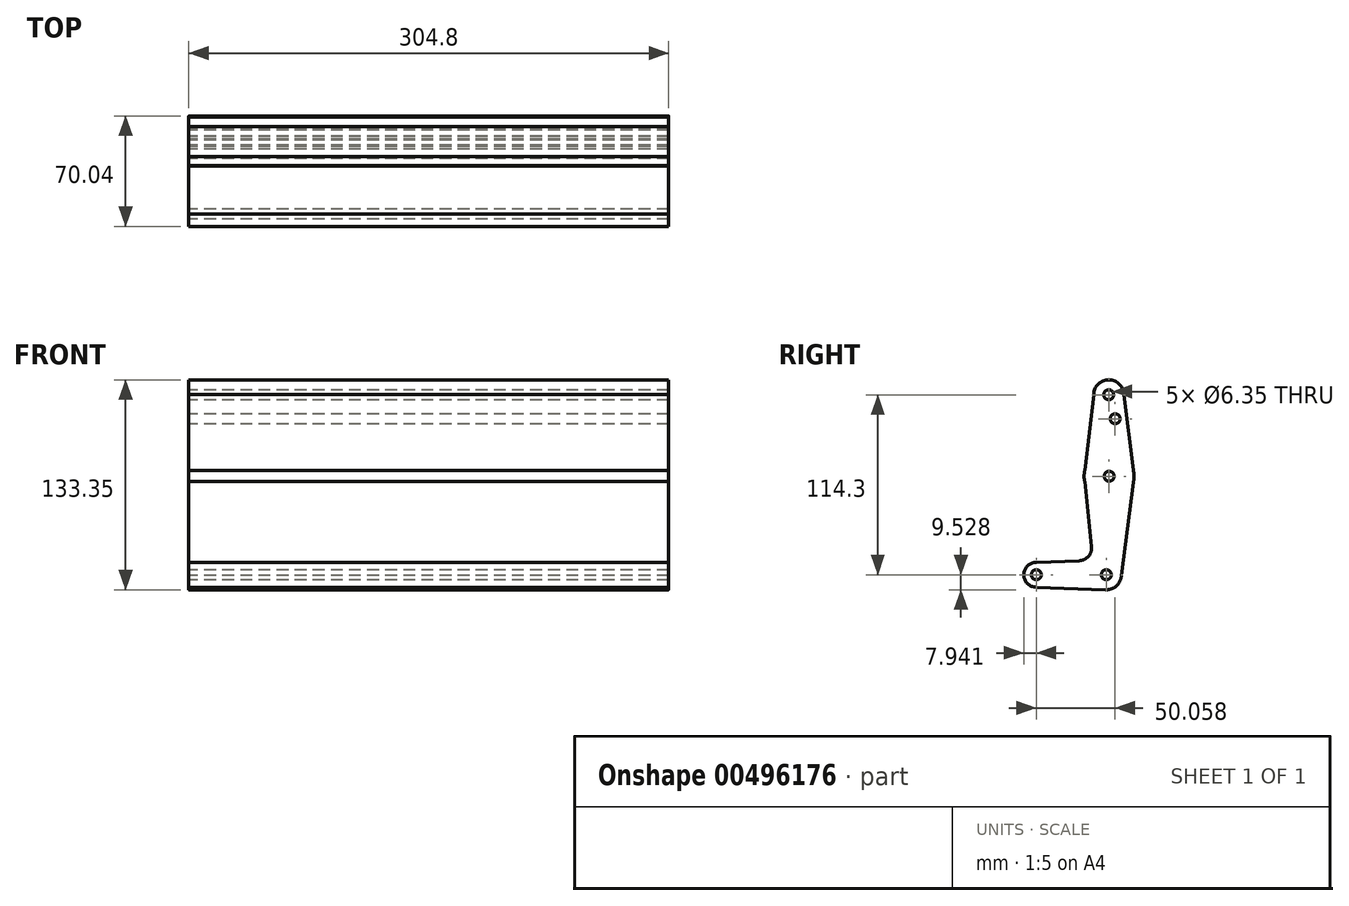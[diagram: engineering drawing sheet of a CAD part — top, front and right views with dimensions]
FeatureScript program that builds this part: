
annotation { "Feature Type Name" : "Feature", "Feature Type Description" : "" }
export const myFeature = defineFeature(function(context is Context, id is Id, definition is map)
    precondition{}
    {
        {
            var Q0;
            Q0=qCreatedBy(makeId("Right.planeOp"),FACE);
            var sketch = newSketch(context, id + "F0", { "sketchPlane" : qUnion([Q0])});
            skCircle(sketch, "E0", {"center": v(-13.33, 51.75) * mm, "radius": 9.53 * mm});
            skCircle(sketch, "E1", {"center": v(-13.33, 51.75) * mm, "radius": 3.18 * mm});
            skCircle(sketch, "E2", {"center": v(-14.88, -62.55) * mm, "radius": 9.53 * mm});
            skCircle(sketch, "E3", {"center": v(-14.88, -62.55) * mm, "radius": 3.18 * mm});
            skCircle(sketch, "E4", {"center": v(-13.1, 0) * mm, "radius": 15.88 * mm});
            skCircle(sketch, "E5", {"center": v(-13.1, 0) * mm, "radius": 3.18 * mm});
            skLineSegment(sketch, "E6", {"start": v(-3.8, 51.75) * mm, "end": v(2.77, 0) * mm});
            skLineSegment(sketch, "E7", {"start": v(-22.63, 53.8) * mm, "end": v(-28.98, 0) * mm});
            skLineSegment(sketch, "E8", {"start": v(-5.36, -62.86) * mm, "end": v(2.77, 0) * mm});
            skCircle(sketch, "E9", {"center": v(-59.33, -62.55) * mm, "radius": 3.18 * mm});
            skCircle(sketch, "E10", {"center": v(-59.33, -62.55) * mm, "radius": 7.94 * mm});
            skLineSegment(sketch, "E11", {"start": v(-14.88, -72.08) * mm, "end": v(-59.33, -70.49) * mm});
            skCircle(sketch, "E12", {"center": v(-9.27, 36.53) * mm, "radius": 3.18 * mm});
            skLineSegment(sketch, "E13", {"start": v(-32.1, -53.64) * mm, "end": v(-59.33, -54.61) * mm});
            skLineSegment(sketch, "E14", {"start": v(-24.23, -44.57) * mm, "end": v(-28.98, 0) * mm});
            skArc(sketch, "E15.filletArc", {"start": v(-32.1, -53.64) * mm, "mid": v(-26.2, -50.82) * mm, "end": v(-24.23, -44.57) * mm});
            skSolve(sketch);
        }
        {
            var Q0;
            Q0 = qSketchRegion(id + "F0", true);
            extrude(context, id + "F1", {"entities" : qUnion([Q0]), "depth" : 304.8 * mm});
        }
    });
